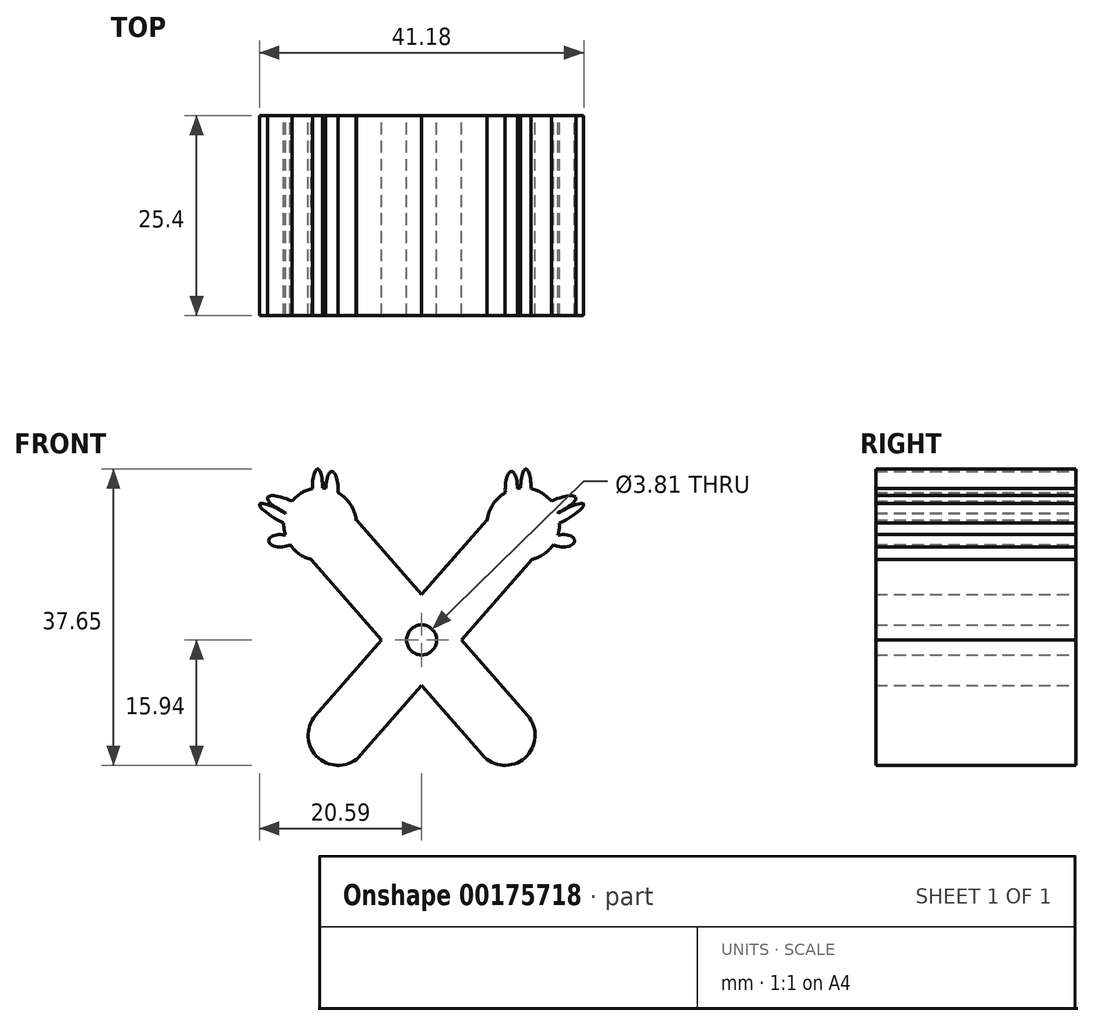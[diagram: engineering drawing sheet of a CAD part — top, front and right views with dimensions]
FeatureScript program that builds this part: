
annotation { "Feature Type Name" : "Feature", "Feature Type Description" : "" }
export const myFeature = defineFeature(function(context is Context, id is Id, definition is map)
    precondition{}
    {
        {
            var Q0;
            Q0=qCreatedBy(makeId("Front.planeOp"),FACE);
            var sketch = newSketch(context, id + "F0", { "sketchPlane" : qUnion([Q0])});
            skLineSegment(sketch, "E0", {"start": v(-8.3, 15.21) * mm, "end": v(13.47, -9.62) * mm});
            skLineSegment(sketch, "E1", {"start": v(-8.3, 15.21) * mm, "end": v(-14.03, 10.2) * mm});
            skLineSegment(sketch, "E2", {"start": v(-14.03, 10.2) * mm, "end": v(7.74, -14.64) * mm});
            skLineSegment(sketch, "E3", {"start": v(7.74, -14.64) * mm, "end": v(13.47, -9.62) * mm});
            skPoint(sketch, "E4", {"position": v(2.59, 2.8) * mm});
            skPoint(sketch, "E5", {"position": v(-3.14, -2.22) * mm});
            skCircle(sketch, "E6", {"center": v(10.6, -12.13) * mm, "radius": 3.81 * mm});
            skPoint(sketch, "E7", {"position": v(-11.16, 12.7) * mm});
            skLineSegment(sketch, "E8", {"start": v(-11.16, 12.7) * mm, "end": v(-12.9, 14.7) * mm});
            skCircle(sketch, "E9", {"center": v(-12.9, 14.7) * mm, "radius": 4.61 * mm});
            skEllipse(sketch, "E10", {"center": v(-17.94, 12.59) * mm, "majorRadius": 1.5 * mm, "minorRadius": 0.8 * mm, "majorAxis": v(1, 0)});
            skEllipse(sketch, "E11", {"center": v(-17.94, 15.75) * mm, "majorRadius": 3.02 * mm, "minorRadius": 0.62 * mm, "majorAxis": v(0.87, -0.5)});
            skPoint(sketch, "E11.centerSnap0", {"position": v(-17.94, 13.38) * mm});
            skEllipse(sketch, "E12", {"center": v(-16.95, 16.92) * mm, "majorRadius": 2.86 * mm, "minorRadius": 0.85 * mm, "majorAxis": v(0.91, -0.41)});
            skEllipse(sketch, "E13", {"center": v(-13.23, 19.3) * mm, "majorRadius": 2.41 * mm, "minorRadius": 0.66 * mm, "majorAxis": v(0, -1)});
            skEllipse(sketch, "E14", {"center": v(-11.4, 19.05) * mm, "majorRadius": 2.34 * mm, "minorRadius": 0.78 * mm, "majorAxis": v(0, -1)});
            skEllipse(sketch, "E15.MirrorC", {"center": v(13.23, 19.3) * mm, "majorRadius": 2.41 * mm, "minorRadius": 0.66 * mm, "majorAxis": v(0, -1)});
            skEllipse(sketch, "E16.MirrorC", {"center": v(11.4, 19.05) * mm, "majorRadius": 2.34 * mm, "minorRadius": 0.78 * mm, "majorAxis": v(0, -1)});
            skCircle(sketch, "E17.MirrorC", {"center": v(12.9, 14.7) * mm, "radius": 4.61 * mm});
            skEllipse(sketch, "E18.MirrorC", {"center": v(16.95, 16.92) * mm, "majorRadius": 2.86 * mm, "minorRadius": 0.85 * mm, "majorAxis": v(-0.91, -0.41)});
            skEllipse(sketch, "E19.MirrorC", {"center": v(17.94, 15.75) * mm, "majorRadius": 3.02 * mm, "minorRadius": 0.62 * mm, "majorAxis": v(-0.87, -0.5)});
            skEllipse(sketch, "E20.MirrorC", {"center": v(17.94, 12.59) * mm, "majorRadius": 1.5 * mm, "minorRadius": 0.8 * mm, "majorAxis": v(-1, 0)});
            skLineSegment(sketch, "E21.MirrorCS", {"start": v(8.3, 15.21) * mm, "end": v(-13.47, -9.62) * mm});
            skLineSegment(sketch, "E22.MirrorCS", {"start": v(8.3, 15.21) * mm, "end": v(14.03, 10.2) * mm});
            skLineSegment(sketch, "E23.MirrorCS", {"start": v(14.03, 10.2) * mm, "end": v(-7.74, -14.64) * mm});
            skLineSegment(sketch, "E24.MirrorCS", {"start": v(-7.74, -14.64) * mm, "end": v(-13.47, -9.62) * mm});
            skCircle(sketch, "E25.MirrorC", {"center": v(-10.6, -12.13) * mm, "radius": 3.81 * mm});
            skPoint(sketch, "E26", {"position": v(-12.9, 21.4) * mm});
            skPoint(sketch, "E27", {"position": v(-10.6, -15.94) * mm});
            skSolve(sketch);
        }
        {
            var Q0;
            Q0 = qSketchRegion(id + "F0", true);
            extrude(context, id + "F1", {"entities" : qUnion([Q0]), "depth" : 25.4 * mm});
        }
        {
            var Q0;
            Q0=makeQuery(id+"F1.opExtrude","CAP_FACE",FACE,{"disambiguationData":[OSD([sQuery(id+"F0.wireOp",EDGE,"E0"),sQuery(id+"F0.wireOp",EDGE,"E1"),sQuery(id+"F0.wireOp",EDGE,"E2"),sQuery(id+"F0.wireOp",EDGE,"E6"),sQuery(id+"F0.wireOp",EDGE,"E9"),sQuery(id+"F0.wireOp",EDGE,"E10"),sQuery(id+"F0.wireOp",EDGE,"E11"),sQuery(id+"F0.wireOp",EDGE,"E12"),sQuery(id+"F0.wireOp",EDGE,"E13"),sQuery(id+"F0.wireOp",EDGE,"E14"),sQuery(id+"F0.wireOp",EDGE,"E15.MirrorC"),sQuery(id+"F0.wireOp",EDGE,"E16.MirrorC"),sQuery(id+"F0.wireOp",EDGE,"E17.MirrorC"),sQuery(id+"F0.wireOp",EDGE,"E18.MirrorC"),sQuery(id+"F0.wireOp",EDGE,"E19.MirrorC"),sQuery(id+"F0.wireOp",EDGE,"E20.MirrorC"),sQuery(id+"F0.wireOp",EDGE,"E21.MirrorCS"),sQuery(id+"F0.wireOp",EDGE,"E22.MirrorCS"),sQuery(id+"F0.wireOp",EDGE,"E23.MirrorCS"),sQuery(id+"F0.wireOp",EDGE,"E25.MirrorC")])],"isStart":true});
            var sketch = newSketch(context, id + "F2", { "sketchPlane" : qUnion([Q0])});
            skCircle(sketch, "E28", {"center": v(0, 0) * mm, "radius": 1.9 * mm});
            skSolve(sketch);
        }
        {
            var Q0;
            Q0 = qSketchRegion(id + "F2", true);
            extrude(context, id + "F3", {"entities" : qUnion([Q0]), "operationType" : NewBodyOperationType.REMOVE, "oppositeDirection" : true, "depth" : 25.4 * mm});
        }
    });
